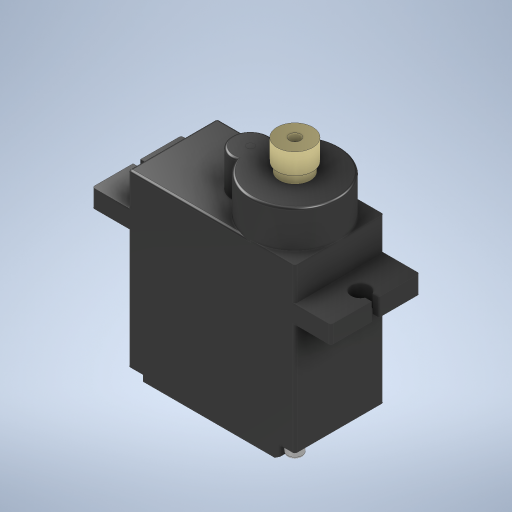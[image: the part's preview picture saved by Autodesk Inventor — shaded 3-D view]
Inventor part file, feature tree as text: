
AUTODESK INVENTOR PART (.ipt)
format: ipt  version: 2023 (Build 270158000, 158)  size: 578,560 bytes
history: native  units: mm
features: extrude x16, sketch x10, fillet x4, other x2, projected_geometry x2
ambient origin geometry x8: Origin, YZ Plane, XZ Plane, XY Plane, X Axis, Y Axis, Z Axis, Center Point
bodies: Body1 (feature_tree)
feature tree (34):
  other  "솔리드1"
  extrude  "돌출1"  Depth=22.5mm
  other  "작업 평면1"
  extrude  "돌출2"  Depth=12.0mm
  extrude  "돌출3"  Depth=24.0mm TaperAngle=0.0deg
  sketch  "스케치4"
  extrude  "돌출6"  [1 undecoded]
  extrude  "돌출7"  Depth=32.2mm
  fillet  "모깎기1"  Radius=12.0mm
  fillet  "모깎기2"  Radius=2.5mm
  sketch  "스케치5"
  extrude  "돌출8"  Depth=2.0mm
  extrude  "돌출9"  Depth=0.5mm
  extrude  "돌출10"  Depth=0.5mm
  extrude  "돌출11"  Depth=2.4mm TaperAngle=0.0deg
  fillet  "모깎기3"  Radius=1.0mm
  sketch  "스케치7"
  extrude  "돌출12"  Depth=1.5mm TaperAngle=0.0deg
  extrude  "돌출13"  Depth=5.0mm
  extrude  "돌출14"  Depth=6.0mm
  extrude  "돌출15"  Depth=5.0mm
  fillet  "모깎기4"  Radius=1.0mm
  extrude  "돌출16"  Depth=5.0mm TaperAngle=0.0deg
  sketch  "스케치12"
  sketch  "스케치13"
  sketch  "스케치14"
  extrude  "돌출18"  Depth=5.01mm TaperAngle=0.0deg
  extrude  "돌출19"  Depth=0.3mm
  sketch  "스케치1"
  sketch  "스케치2"
  sketch  "스케치3"
  projected_geometry  "투영된 루프1"
  projected_geometry  "투영된 루프2"
  sketch  "스케치6"
note: 1 required parameter value undecoded (feature->parameter linkage not recoverable at this tier; creation-order binding heuristic only, values carry confidence <= 0.55)
